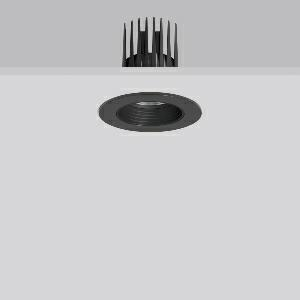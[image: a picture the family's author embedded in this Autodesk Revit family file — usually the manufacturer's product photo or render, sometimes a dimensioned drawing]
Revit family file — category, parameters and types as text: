
# Revit family: heledon_mini_e_901745_003_1_b263
name_source: partatom
category: Lighting Fixtures
units: mm (PartAtom-declared; Revit-internal decimal feet)

## family parameters
Cut with Voids When Loaded = No
Host = Face
Light Source = No
Part Type = Normal
Room Calculation Point = No
Round Connector Dimension = Use Diameter
Shared = No

## types (1)
- HELEDON mini E (1 x LED Modul 940, 2150 lm, 4000)
    Apparent Load = 20 VA
    Approval mark = CE
    CIE Flux Codes = 98 100 100 100 100
    Color Rendering = 92
    Color Temperature = 4000
    Default Elevation = 1800 mm
    Description = Series: HELEDON mini
Round recessed downlight. Housing: die-cast aluminium, powder-coated. Black plastic ring and recessed LED to prevent glare from the side. Optical assembly with lens made of plastic (polycarbonate) for the best homogeneous light distribution - can be changed without tools. Best colour rendering index Ra>90. Suitable for Recessed ceiling mounting. Installation without tools thanks to spring fastening system. Including separate LED converter with connecting cable 600 mm.High quality converter without flickering and stroboscopic effect. Through-wiring box (5 pole) available as accessory. The following accessories can be mounted without use of tools: interchangeable lenses, decorative glasses, honeycomb louvre, clear and frosted diffusers, white interchangeable plastic ring. 
Colour: deep black, matt (RAL 9005)
Diameter: 124 mm
Height: 3 mm
Cut-out diameter: 114 mm
Recess height: 170 mm
Luminaire: recess height: 120 mm
Lamp: LED
Socket: without socket
Colour temperature: 4000K
Colour rendering index (CRI): 92
System power: 20 W
Rated luminous flux: 2150 lm
Luminous efficiency: 108 lm/W
Control gear: Regulated power supply
Protection class: II
Type of protection: IP 20
    Height = 0 mm  [stored 0 ft]
    Lamp = 1 x LED Modul 940
    Lamp Light Flux = 2150 lm
    Lamp count = 1
    Length = 124 mm
    Lifetime = 50000 h
    Luminous efficacy = 108 lm/W
    Manufacturer = RZB
    ModVariant = No
    Model = 901745.003.1
    Mounting Place = Ceiling
    Mounting Type = Recessed
    Number of Poles = 1
    OnlyDefault = Yes
    Power Factor = 1
    Product Name = HELEDON mini E
    Product group = Recessed downlights
    ProductGroupID = 402
    Protection Class = Protection class II
    Protection Degree = IP 20
    RLX_Detail_Level = 1
    RLX_Emergency_Light_Flux = 0 lm
    RLX_Emergency_Type = 0
    RLX_Emergency_Type_DB = No
    RlxData = <blob elided: 127093 chars, md5=06df1584>
    Socket = socket
    Standby Power = 0 W
    System Light Flux = 2150 lm
    System Power = 20 W
    Type Comments = Product without accessories
    Type Image = 901656.003.jpg
    URL = http://relux.com
    VarID = ---
    Voltage = 230 V
    Voltage Range = 220-240 V
    Weight = 0.00 kg
    Width = 0 mm  [stored 0 ft]

note: [stored X ft] marks values corroborated as IEEE doubles in the binary element streams (Revit-internal decimal feet)

## geometry (parser evidence)
native form markers: Blend x4, Sweep x10
no freeform markers — native parametric forms only
